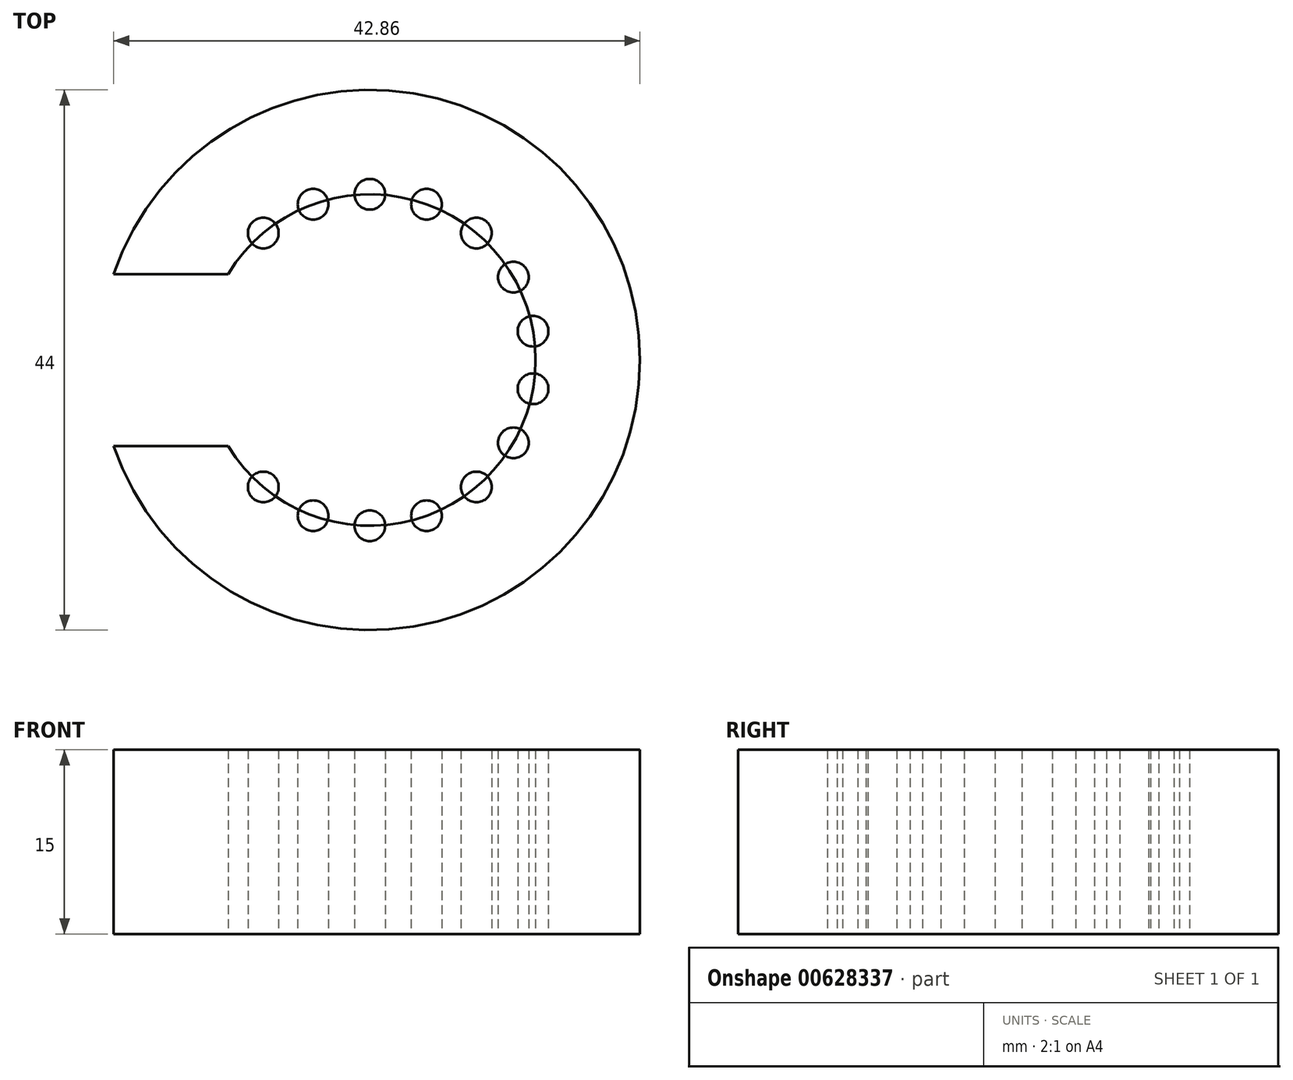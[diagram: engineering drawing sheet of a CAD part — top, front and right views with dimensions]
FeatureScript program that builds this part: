
annotation { "Feature Type Name" : "Feature", "Feature Type Description" : "" }
export const myFeature = defineFeature(function(context is Context, id is Id, definition is map)
    precondition{}
    {
        {
            var Q0;
            Q0=qCreatedBy(makeId("Top.planeOp"),FACE);
            var sketch = newSketch(context, id + "F0", { "sketchPlane" : qUnion([Q0])});
            skCircle(sketch, "E0", {"center": v(0, 0) * mm, "radius": 13.5 * mm});
            skCircle(sketch, "E1", {"center": v(0, 0) * mm, "radius": 22 * mm});
            skLineSegment(sketch, "E2", {"start": v(0, 0) * mm, "end": v(0, 7) * mm, "construction": true});
            skLineSegment(sketch, "E3", {"start": v(0, 0) * mm, "end": v(0, -7) * mm, "construction": true});
            skLineSegment(sketch, "E4", {"start": v(0, -7) * mm, "end": v(-20, -7) * mm, "construction": true});
            skLineSegment(sketch, "E5", {"start": v(0, 7) * mm, "end": v(-20, 7) * mm, "construction": true});
            skLineSegment(sketch, "E6", {"start": v(-20.86, 7) * mm, "end": v(-11.54, 7) * mm});
            skLineSegment(sketch, "E7", {"start": v(-20.86, -7) * mm, "end": v(-11.54, -7) * mm});
            skSolve(sketch);
        }
        {
            var Q0;
            {var subQ0=sQuery(id+"F0.wireOp",EDGE,"E6");Q0=makeQuery(id+"F0.imprint","IMPRINT",FACE,{"disambiguationData":[TD([[makeQuery(id+"F0.imprint","IMPRINT",EDGE,{"derivedFrom":subQ0}),1.0]])]});}
            extrude(context, id + "F1", {"entities" : qUnion([Q0]), "depth" : 15 * mm, "offsetDistance" : 25 * mm});
        }
        {
            var Q0;
            Q0=qCreatedBy(makeId("Top.planeOp"),FACE);
            var sketch = newSketch(context, id + "F2", { "sketchPlane" : qUnion([Q0])});
            skLineSegment(sketch, "E8", {"start": v(0, 0) * mm, "end": v(0, 13.5) * mm, "construction": true});
            skCircle(sketch, "E9", {"center": v(0, 13.5) * mm, "radius": 1.25 * mm});
            skSolve(sketch);
        }
        {
            var Q0;
            Q0=qSketchRegion(id+"F2",true);
            extrude(context, id + "F3", {"entities" : qUnion([Q0]), "depth" : 15 * mm, "offsetDistance" : 25 * mm});
        }
        {
            var Q0;
            Q0=qCreatedBy(makeId("Right.planeOp"),FACE);
            var sketch = newSketch(context, id + "F4", { "sketchPlane" : qUnion([Q0])});
            skLineSegment(sketch, "E10", {"start": v(0, 0) * mm, "end": v(0, 10) * mm});
            skSolve(sketch);
        }
        {
            var Q0;
            Q0=makeQuery(id+"F3.opExtrude","SWEPT_BODY",BODY,{"disambiguationData":[OSD([sQuery(id+"F2.wireOp",EDGE,"E9")])]});
            var Q1;
            Q1=sQuery(id+"F4.wireOp",EDGE,"E10");
            circularPattern(context, id + "F5", {"entities" : qUnion([Q0]), "axis" : qUnion([Q1]), "angle" : 360 * degree, "instanceCount" : 18, "equalSpace" : true});
        }
        {
            var Q0;
            Q0=makeQuery(id+"F5.opPattern","COPY",BODY,{"derivedFrom":makeQuery(id+"F3.opExtrude","SWEPT_BODY",BODY,{"disambiguationData":[OSD([sQuery(id+"F2.wireOp",EDGE,"E9")])]}),"instanceName":"3"});
            var Q1;
            Q1=makeQuery(id+"F5.opPattern","COPY",BODY,{"derivedFrom":makeQuery(id+"F3.opExtrude","SWEPT_BODY",BODY,{"disambiguationData":[OSD([sQuery(id+"F2.wireOp",EDGE,"E9")])]}),"instanceName":"4"});
            var Q2;
            Q2=makeQuery(id+"F5.opPattern","COPY",BODY,{"derivedFrom":makeQuery(id+"F3.opExtrude","SWEPT_BODY",BODY,{"disambiguationData":[OSD([sQuery(id+"F2.wireOp",EDGE,"E9")])]}),"instanceName":"5"});
            var Q3;
            Q3=makeQuery(id+"F5.opPattern","COPY",BODY,{"derivedFrom":makeQuery(id+"F3.opExtrude","SWEPT_BODY",BODY,{"disambiguationData":[OSD([sQuery(id+"F2.wireOp",EDGE,"E9")])]}),"instanceName":"6"});
            deleteBodies(context, id + "F6", {"entities" : qUnion([Q0, Q1, Q2, Q3])});
        }
        {
            var Q0;
            Q0=qCreatedBy(makeId("Top.planeOp"),FACE);
            var sketch = newSketch(context, id + "F7", { "sketchPlane" : qUnion([Q0])});
            skCircle(sketch, "E11.cCircle", {"center": v(0, 0) * mm, "radius": 19.04 * mm, "construction": true});
            skLineSegment(sketch, "E11.0", {"start": v(-11, 19.04) * mm, "end": v(11, 19.04) * mm});
            skLineSegment(sketch, "E11.1", {"start": v(11, 19.04) * mm, "end": v(21.98, 0) * mm});
            skLineSegment(sketch, "E11.2", {"start": v(21.98, 0) * mm, "end": v(11, -19.04) * mm});
            skLineSegment(sketch, "E11.3", {"start": v(11, -19.04) * mm, "end": v(-11, -19.04) * mm});
            skLineSegment(sketch, "E11.4", {"start": v(-11, -19.04) * mm, "end": v(-21.98, 0) * mm});
            skLineSegment(sketch, "E11.5", {"start": v(-21.98, 0) * mm, "end": v(-11, 19.04) * mm});
            skPoint(sketch, "E11.0.midPoint", {"position": v(0, 19.04) * mm});
            skSolve(sketch);
        }
        {
            var Q0;
            Q0 = qSketchRegion(id + "F7", true);
            extrude(context, id + "F8", {"entities" : qUnion([Q0]), "depth" : 15 * mm, "offsetDistance" : 25 * mm});
        }
        {
            var Q0;
            Q0=makeQuery(id+"F3.opExtrude","SWEPT_BODY",BODY,{"disambiguationData":[OSD([sQuery(id+"F2.wireOp",EDGE,"E9")])]});
            var Q1;
            Q1=makeQuery(id+"F8.opExtrude","SWEPT_BODY",BODY,{"disambiguationData":[OSD([sQuery(id+"F7.wireOp",EDGE,"E11.0"),sQuery(id+"F7.wireOp",EDGE,"E11.1"),sQuery(id+"F7.wireOp",EDGE,"E11.2"),sQuery(id+"F7.wireOp",EDGE,"E11.3"),sQuery(id+"F7.wireOp",EDGE,"E11.4"),sQuery(id+"F7.wireOp",EDGE,"E11.5")])]});
            booleanBodies(context, id + "F9", {"operationType" : BooleanOperationType.INTERSECTION, "tools" : qUnion([Q0, Q1])});
        }
    });
